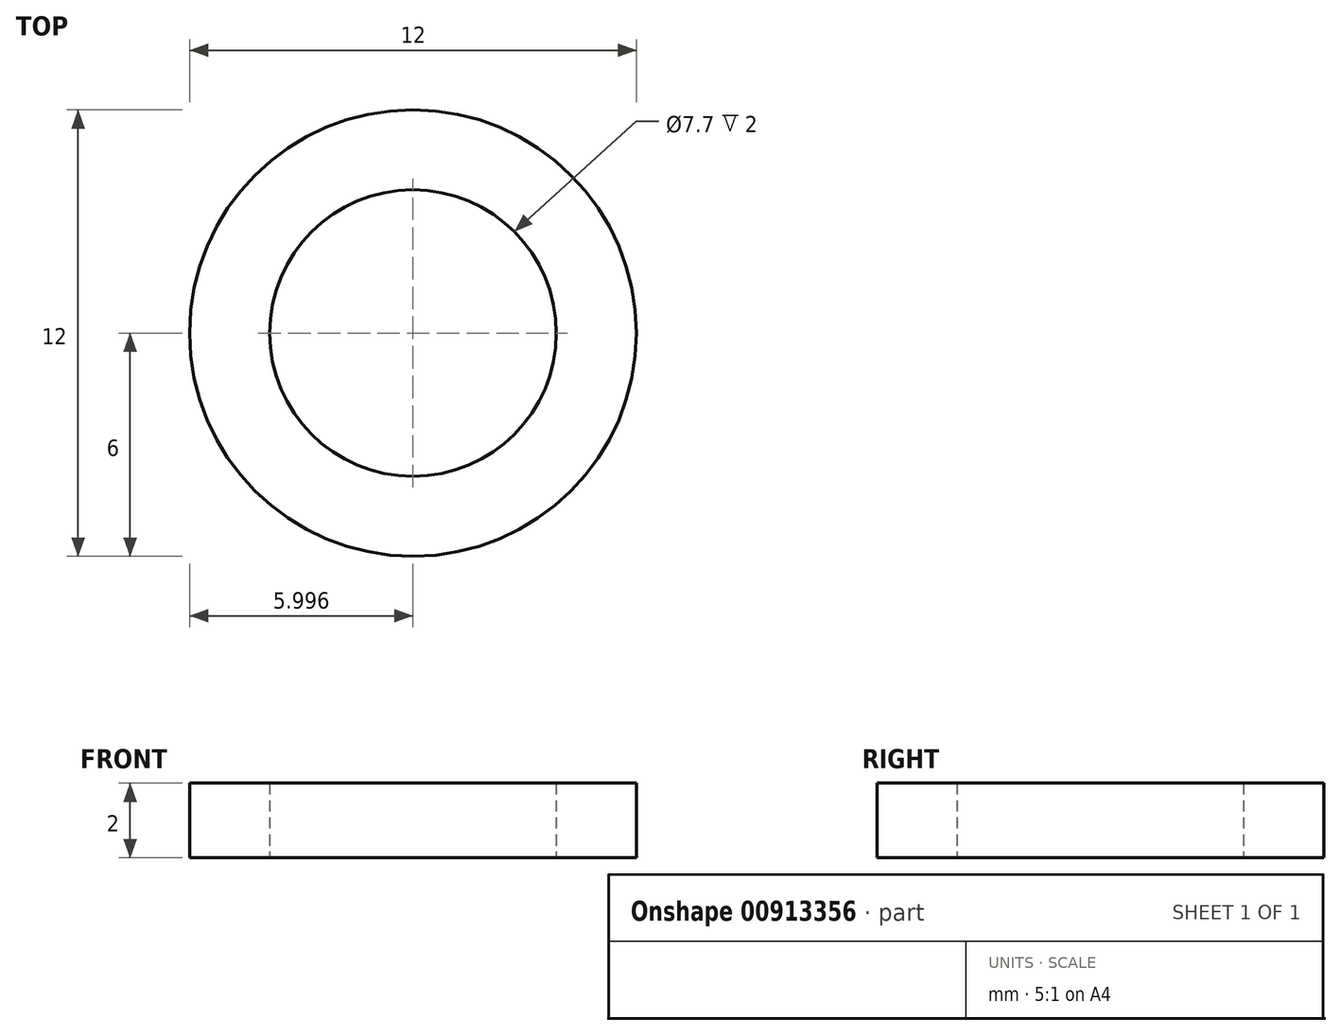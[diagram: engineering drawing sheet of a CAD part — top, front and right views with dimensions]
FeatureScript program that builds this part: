
annotation { "Feature Type Name" : "Feature", "Feature Type Description" : "" }
export const myFeature = defineFeature(function(context is Context, id is Id, definition is map)
    precondition{}
    {
        {
            var Q0;
            Q0=qCreatedBy(makeId("Top.planeOp"),FACE);
            var sketch = newSketch(context, id + "F0", { "sketchPlane" : qUnion([Q0])});
            skCircle(sketch, "E0", {"center": v(18.42, 0) * mm, "radius": 6 * mm});
            skCircle(sketch, "E1", {"center": v(18.42, 0) * mm, "radius": 3.85 * mm});
            skSolve(sketch);
        }
        {
            var Q0;
            Q0 = qSketchRegion(id + "F0", true);
            extrude(context, id + "F1", {"entities" : qUnion([Q0]), "depth" : 2 * mm, "offsetDistance" : 25 * mm});
        }
    });
